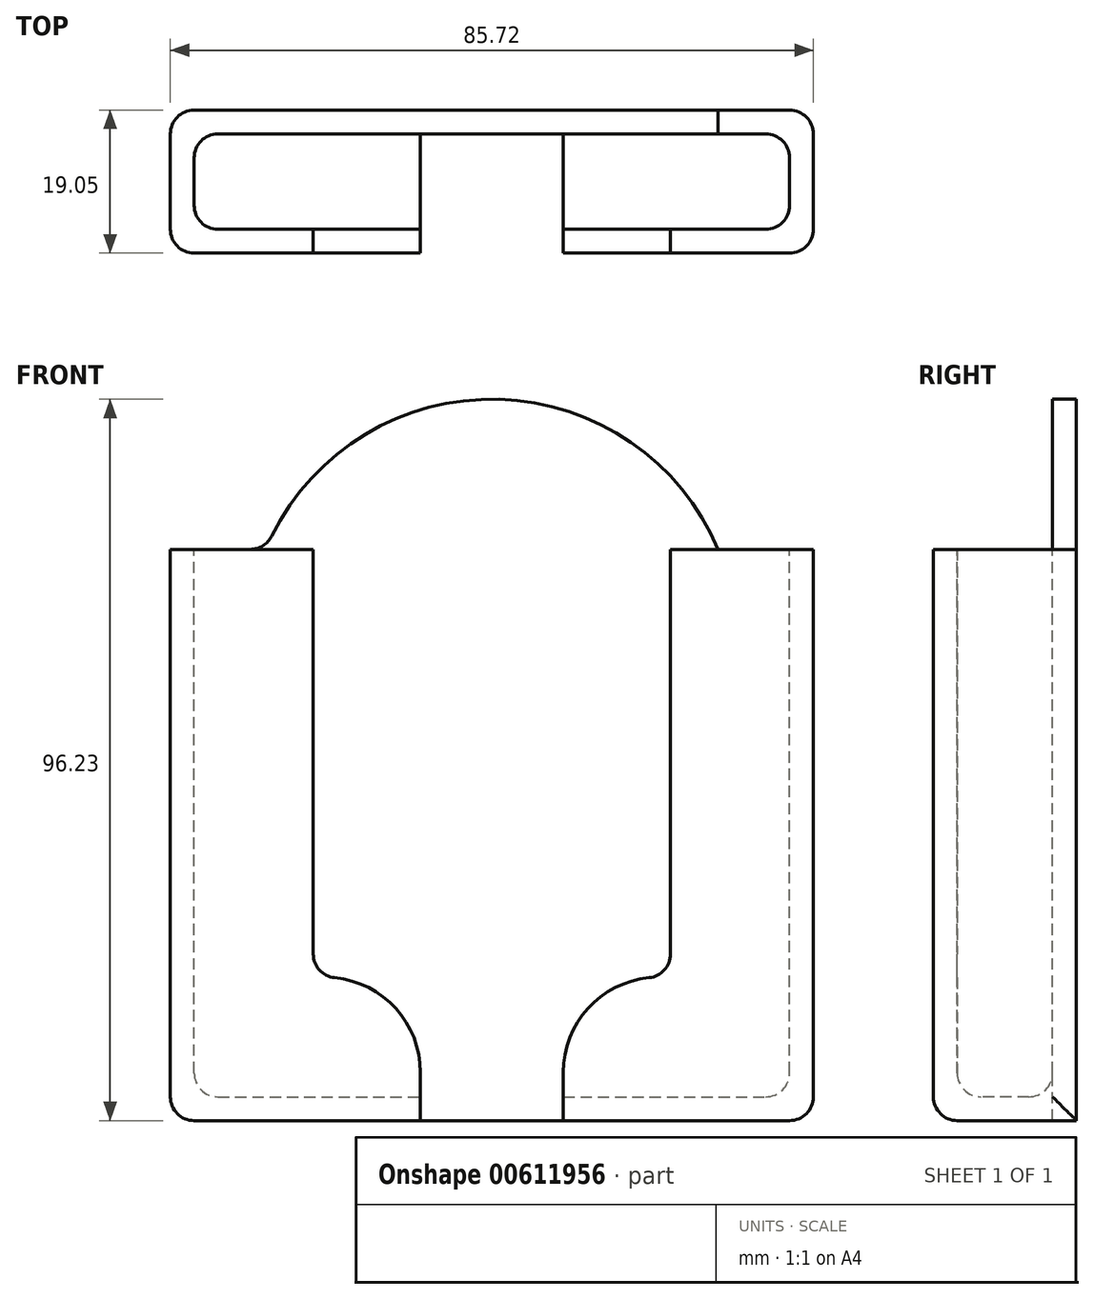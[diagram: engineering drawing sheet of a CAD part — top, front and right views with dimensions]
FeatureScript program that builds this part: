
annotation { "Feature Type Name" : "Feature", "Feature Type Description" : "" }
export const myFeature = defineFeature(function(context is Context, id is Id, definition is map)
    precondition{}
    {
        {
            var Q0;
            Q0=qCreatedBy(makeId("Front.planeOp"),FACE);
            var sketch = newSketch(context, id + "F0", { "sketchPlane" : qUnion([Q0])});
            skLineSegment(sketch, "E0.bottom", {"start": v(0, 0) * mm, "end": v(85.73, 0) * mm});
            skLineSegment(sketch, "E0.top", {"start": v(0, 76.2) * mm, "end": v(85.72, 76.2) * mm});
            skLineSegment(sketch, "E0.left", {"start": v(0, 0) * mm, "end": v(0, 76.2) * mm});
            skLineSegment(sketch, "E0.right", {"start": v(85.73, 0) * mm, "end": v(85.72, 76.2) * mm});
            skSolve(sketch);
        }
        {
            var Q0;
            Q0 = qSketchRegion(id + "F0", true);
            extrude(context, id + "F1", {"entities" : qUnion([Q0]), "depth" : 19.05 * mm, "offsetDistance" : 25.4 * mm});
        }
        {
            var Q0;
            Q0=makeQuery(id+"F1.opExtrude","SWEPT_FACE",FACE,{"disambiguationData":[OSD([sQuery(id+"F0.wireOp",EDGE,"E0.top")])]});
            shell(context, id + "F2", {"entities" : qUnion([Q0]), "thickness" : 3.17 * mm});
        }
        {
            var Q0;
            Q0=makeQuery(id+"F1.opExtrude","CAP_FACE",FACE,{"disambiguationData":[OSD([sQuery(id+"F0.wireOp",EDGE,"E0.bottom"),sQuery(id+"F0.wireOp",EDGE,"E0.top"),sQuery(id+"F0.wireOp",EDGE,"E0.left"),sQuery(id+"F0.wireOp",EDGE,"E0.right")])],"isStart":false});
            var sketch = newSketch(context, id + "F3", { "sketchPlane" : qUnion([Q0])});
            skPoint(sketch, "E1.startSnap0", {"position": v(42.86, 76.2) * mm});
            skLineSegment(sketch, "E2.bottom", {"start": v(19.05, 76.2) * mm, "end": v(42.86, 76.2) * mm});
            skLineSegment(sketch, "E2.top", {"start": v(19.05, 19.05) * mm, "end": v(33.34, 19.05) * mm});
            skLineSegment(sketch, "E2.left", {"start": v(19.05, 76.2) * mm, "end": v(19.05, 19.05) * mm});
            skLineSegment(sketch, "E3.top", {"start": v(33.34, 0) * mm, "end": v(42.86, 0) * mm});
            skLineSegment(sketch, "E3.left", {"start": v(33.34, 19.05) * mm, "end": v(33.34, 0) * mm});
            skLineSegment(sketch, "E4", {"start": v(42.86, 76.2) * mm, "end": v(42.86, 0) * mm});
            skLineSegment(sketch, "E5", {"start": v(42.86, 99.28) * mm, "end": v(42.86, -20.52) * mm, "construction": true});
            skLineSegment(sketch, "E6.MirrorCS", {"start": v(52.39, 19.05) * mm, "end": v(52.39, 0) * mm});
            skLineSegment(sketch, "E7.MirrorCS", {"start": v(66.67, 76.2) * mm, "end": v(66.67, 19.05) * mm});
            skLineSegment(sketch, "E8.MirrorCS", {"start": v(66.67, 19.05) * mm, "end": v(52.39, 19.05) * mm});
            skLineSegment(sketch, "E9.MirrorCS", {"start": v(66.67, 76.2) * mm, "end": v(42.86, 76.2) * mm});
            skLineSegment(sketch, "E10.MirrorCS", {"start": v(52.39, 0) * mm, "end": v(42.86, 0) * mm});
            skSolve(sketch);
        }
        {
            var Q0;
            Q0 = qSketchRegion(id + "F3", true);
            var Q1;
            {var subQ0=sQuery(id+"F0.wireOp",EDGE,"E0.right");var subQ1=sQuery(id+"F0.wireOp",EDGE,"E0.left");var subQ2=sQuery(id+"F0.wireOp",EDGE,"E0.top");var subQ3=sQuery(id+"F0.wireOp",EDGE,"E0.bottom");Q1=makeQuery(id+"F2.opShell","OFFSET_FACE",FACE,{"disambiguationData":[OSD([subQ3,subQ2,subQ1,subQ0]),TDD([makeQuery(id+"F1.opExtrude","CAP_FACE",FACE,{"disambiguationData":[OSD([subQ3,subQ2,subQ1,subQ0])],"isStart":true})])]});}
            extrude(context, id + "F4", {"entities" : qUnion([Q0]), "operationType" : NewBodyOperationType.REMOVE, "endBound" : BoundingType.UP_TO_SURFACE, "oppositeDirection" : true, "depth" : 25.4 * mm, "endBoundEntityFace" : qUnion([Q1]), "offsetDistance" : 25.4 * mm});
        }
        {
            var Q0;
            Q0=makeQuery(id+"F1.opExtrude","CAP_FACE",FACE,{"disambiguationData":[OSD([sQuery(id+"F0.wireOp",EDGE,"E0.bottom"),sQuery(id+"F0.wireOp",EDGE,"E0.top"),sQuery(id+"F0.wireOp",EDGE,"E0.left"),sQuery(id+"F0.wireOp",EDGE,"E0.right")])],"isStart":true});
            var sketch = newSketch(context, id + "F5", { "sketchPlane" : qUnion([Q0])});
            skArc(sketch, "E11", {"start": v(-12.7, 76.2) * mm, "mid": v(-42.86, 96.23) * mm, "end": v(-73.02, 76.2) * mm});
            skSolve(sketch);
        }
        {
            var Q0;
            {var subQ0=sQuery(id+"F5.wireOp",EDGE,"E11");Q0=makeQuery(id+"F5.imprint","IMPRINT",FACE,{"disambiguationData":[TD([[makeQuery(id+"F5.imprint","IMPRINT",EDGE,{"derivedFrom":subQ0}),1.0]])]});}
            var Q1;
            {var subQ0=sQuery(id+"F0.wireOp",EDGE,"E0.right");var subQ1=sQuery(id+"F0.wireOp",EDGE,"E0.left");var subQ2=sQuery(id+"F0.wireOp",EDGE,"E0.top");var subQ3=sQuery(id+"F0.wireOp",EDGE,"E0.bottom");Q1=makeQuery(id+"F4.boolean.opBoolean","MERGE",FACE,{"derivedFrom":[makeQuery(id+"F2.opShell","OFFSET_FACE",FACE,{"disambiguationData":[OSD([subQ3,subQ2,subQ1,subQ0]),TDD([makeQuery(id+"F1.opExtrude","CAP_FACE",FACE,{"disambiguationData":[OSD([subQ3,subQ2,subQ1,subQ0])],"isStart":true})])]}),makeQuery(id+"F4.opExtrude","CAP_FACE",FACE,{"disambiguationData":[OSD([subQ3,subQ2,subQ1,subQ0])],"isStart":false})]});}
            extrude(context, id + "F6", {"entities" : qUnion([Q0]), "operationType" : NewBodyOperationType.ADD, "endBound" : BoundingType.UP_TO_SURFACE, "oppositeDirection" : true, "depth" : 25.4 * mm, "endBoundEntityFace" : qUnion([Q1]), "offsetDistance" : 25.4 * mm});
        }
        {
            var Q0;
            {var subQ0=sQuery(id+"F0.wireOp",EDGE,"E0.left");Q0=makeQuery(id+"F2.opShell","OFFSET_EDGE",EDGE,{"disambiguationData":[OSD([subQ0]),TDD([makeQuery(id+"F1.opExtrude","CAP_EDGE",EDGE,{"disambiguationData":[OSD([subQ0])],"isStart":true})])]});}
            var Q1;
            {var subQ0=sQuery(id+"F0.wireOp",EDGE,"E0.left");Q1=makeQuery(id+"F2.opShell","OFFSET_EDGE",EDGE,{"disambiguationData":[OSD([subQ0]),TDD([makeQuery(id+"F1.opExtrude","CAP_EDGE",EDGE,{"disambiguationData":[OSD([subQ0])],"isStart":false})])]});}
            var Q2;
            {var subQ0=sQuery(id+"F5.wireOp",EDGE,"E11");var subQ1=sQuery(id+"F0.wireOp",EDGE,"E0.top");Q2=makeQuery(id+"F6.opExtrude","SWEPT_EDGE",EDGE,{"disambiguationData":[OSD([subQ1,subQ0]),TDD([makeQuery(id+"F5.imprint","INTERSECT",VERTEX,{"disambiguationData":[OD(0.0)],"derivedFrom":[makeQuery(id+"F1.opExtrude","CAP_EDGE",EDGE,{"disambiguationData":[OSD([subQ1])],"isStart":true}),subQ0]})])]});}
            var Q3;
            {var subQ0=sQuery(id+"F5.wireOp",EDGE,"E11");var subQ1=sQuery(id+"F0.wireOp",EDGE,"E0.top");Q3=makeQuery(id+"F6.opExtrude","SWEPT_EDGE",EDGE,{"disambiguationData":[OSD([subQ1,subQ0]),TDD([makeQuery(id+"F5.imprint","INTERSECT",VERTEX,{"disambiguationData":[OD(1.0)],"derivedFrom":[makeQuery(id+"F1.opExtrude","CAP_EDGE",EDGE,{"disambiguationData":[OSD([subQ1])],"isStart":true}),subQ0]})])]});}
            var Q4;
            {var subQ0=sQuery(id+"F0.wireOp",EDGE,"E0.right");Q4=makeQuery(id+"F2.opShell","OFFSET_EDGE",EDGE,{"disambiguationData":[OSD([subQ0]),TDD([makeQuery(id+"F1.opExtrude","CAP_EDGE",EDGE,{"disambiguationData":[OSD([subQ0])],"isStart":true})])]});}
            var Q5;
            {var subQ0=sQuery(id+"F0.wireOp",EDGE,"E0.right");Q5=makeQuery(id+"F2.opShell","OFFSET_EDGE",EDGE,{"disambiguationData":[OSD([subQ0]),TDD([makeQuery(id+"F1.opExtrude","CAP_EDGE",EDGE,{"disambiguationData":[OSD([subQ0])],"isStart":false})])]});}
            var Q6;
            Q6=makeQuery(id+"F4.boolean.opBoolean","COPY",EDGE,{"derivedFrom":makeQuery(id+"F4.opExtrude","SWEPT_EDGE",EDGE,{"disambiguationData":[OSD([sQuery(id+"F3.wireOp",EDGE,"E7.MirrorCS"),sQuery(id+"F3.wireOp",EDGE,"E8.MirrorCS")])]})});
            var Q7;
            Q7=makeQuery(id+"F4.boolean.opBoolean","COPY",EDGE,{"derivedFrom":makeQuery(id+"F4.opExtrude","SWEPT_EDGE",EDGE,{"disambiguationData":[OSD([sQuery(id+"F3.wireOp",EDGE,"E2.top"),sQuery(id+"F3.wireOp",EDGE,"E2.left")])]})});
            var Q8;
            {var subQ1=sQuery(id+"F0.wireOp",EDGE,"E0.left");var subQ3=sQuery(id+"F0.wireOp",EDGE,"E0.bottom");Q8=makeQuery(id+"F4.boolean.opBoolean","SPLIT",EDGE,{"disambiguationData":[TD([makeQuery(id+"F2.opShell","OFFSET_FACE",FACE,{"disambiguationData":[OSD([subQ1])]})])],"derivedFrom":makeQuery(id+"F2.opShell","OFFSET_EDGE",EDGE,{"disambiguationData":[OSD([subQ3]),TDD([makeQuery(id+"F1.opExtrude","CAP_EDGE",EDGE,{"disambiguationData":[OSD([subQ3])],"isStart":true})])]})});}
            var Q9;
            Q9=makeQuery(id+"F2.opShell","OFFSET_EDGE",EDGE,{"disambiguationData":[OSD([sQuery(id+"F0.wireOp",EDGE,"E0.bottom"),sQuery(id+"F0.wireOp",EDGE,"E0.left")])]});
            var Q10;
            {var subQ0=sQuery(id+"F0.wireOp",EDGE,"E0.bottom");var subQ2=sQuery(id+"F0.wireOp",EDGE,"E0.left");Q10=makeQuery(id+"F4.boolean.opBoolean","SPLIT",EDGE,{"disambiguationData":[TD([makeQuery(id+"F2.opShell","OFFSET_FACE",FACE,{"disambiguationData":[OSD([subQ2])]})])],"derivedFrom":makeQuery(id+"F2.opShell","OFFSET_EDGE",EDGE,{"disambiguationData":[OSD([subQ0]),TDD([makeQuery(id+"F1.opExtrude","CAP_EDGE",EDGE,{"disambiguationData":[OSD([subQ0])],"isStart":false})])]})});}
            var Q11;
            {var subQ0=sQuery(id+"F0.wireOp",EDGE,"E0.right");var subQ3=sQuery(id+"F0.wireOp",EDGE,"E0.bottom");Q11=makeQuery(id+"F4.boolean.opBoolean","SPLIT",EDGE,{"disambiguationData":[TD([makeQuery(id+"F2.opShell","OFFSET_FACE",FACE,{"disambiguationData":[OSD([subQ0])]})])],"derivedFrom":makeQuery(id+"F2.opShell","OFFSET_EDGE",EDGE,{"disambiguationData":[OSD([subQ3]),TDD([makeQuery(id+"F1.opExtrude","CAP_EDGE",EDGE,{"disambiguationData":[OSD([subQ3])],"isStart":true})])]})});}
            var Q12;
            {var subQ0=sQuery(id+"F0.wireOp",EDGE,"E0.bottom");var subQ1=sQuery(id+"F0.wireOp",EDGE,"E0.right");Q12=makeQuery(id+"F4.boolean.opBoolean","SPLIT",EDGE,{"disambiguationData":[TD([makeQuery(id+"F2.opShell","OFFSET_FACE",FACE,{"disambiguationData":[OSD([subQ1])]})])],"derivedFrom":makeQuery(id+"F2.opShell","OFFSET_EDGE",EDGE,{"disambiguationData":[OSD([subQ0]),TDD([makeQuery(id+"F1.opExtrude","CAP_EDGE",EDGE,{"disambiguationData":[OSD([subQ0])],"isStart":false})])]})});}
            var Q13;
            Q13=makeQuery(id+"F2.opShell","OFFSET_EDGE",EDGE,{"disambiguationData":[OSD([sQuery(id+"F0.wireOp",EDGE,"E0.bottom"),sQuery(id+"F0.wireOp",EDGE,"E0.right")])]});
            var Q14;
            Q14=makeQuery(id+"F1.opExtrude","CAP_EDGE",EDGE,{"disambiguationData":[OSD([sQuery(id+"F0.wireOp",EDGE,"E0.right")])],"isStart":false});
            var Q15;
            Q15=makeQuery(id+"F1.opExtrude","CAP_EDGE",EDGE,{"disambiguationData":[OSD([sQuery(id+"F0.wireOp",EDGE,"E0.right")])],"isStart":true});
            var Q16;
            Q16=makeQuery(id+"F1.opExtrude","CAP_EDGE",EDGE,{"disambiguationData":[OSD([sQuery(id+"F0.wireOp",EDGE,"E0.left")])],"isStart":true});
            var Q17;
            Q17=makeQuery(id+"F1.opExtrude","CAP_EDGE",EDGE,{"disambiguationData":[OSD([sQuery(id+"F0.wireOp",EDGE,"E0.left")])],"isStart":false});
            var Q18;
            Q18=makeQuery(id+"F1.opExtrude","SWEPT_EDGE",EDGE,{"disambiguationData":[OSD([sQuery(id+"F0.wireOp",EDGE,"E0.bottom"),sQuery(id+"F0.wireOp",EDGE,"E0.left")])]});
            var Q19;
            {var subQ0=sQuery(id+"F0.wireOp",EDGE,"E0.bottom");var subQ1=sQuery(id+"F0.wireOp",EDGE,"E0.right");Q19=makeQuery(id+"F4.boolean.opBoolean","SPLIT",EDGE,{"disambiguationData":[TD([makeQuery(id+"F1.opExtrude","SWEPT_FACE",FACE,{"disambiguationData":[OSD([subQ1])]})])],"derivedFrom":makeQuery(id+"F1.opExtrude","CAP_EDGE",EDGE,{"disambiguationData":[OSD([subQ0])],"isStart":false})});}
            var Q20;
            {var subQ0=sQuery(id+"F0.wireOp",EDGE,"E0.bottom");var subQ1=sQuery(id+"F0.wireOp",EDGE,"E0.left");Q20=makeQuery(id+"F4.boolean.opBoolean","SPLIT",EDGE,{"disambiguationData":[TD([makeQuery(id+"F1.opExtrude","SWEPT_FACE",FACE,{"disambiguationData":[OSD([subQ1])]})])],"derivedFrom":makeQuery(id+"F1.opExtrude","CAP_EDGE",EDGE,{"disambiguationData":[OSD([subQ0])],"isStart":false})});}
            var Q21;
            Q21=makeQuery(id+"F1.opExtrude","SWEPT_EDGE",EDGE,{"disambiguationData":[OSD([sQuery(id+"F0.wireOp",EDGE,"E0.bottom"),sQuery(id+"F0.wireOp",EDGE,"E0.right")])]});
            fillet(context, id + "F7", {"entities" : qUnion([Q0, Q1, Q2, Q3, Q4, Q5, Q6, Q7, Q8, Q9, Q10, Q11, Q12, Q13, Q14, Q15, Q16, Q17, Q18, Q19, Q20, Q21]), "radius" : 3.17 * mm, "tangentPropagation" : true, "allowEdgeOverflow" : false});
        }
        {
            var Q0;
            Q0=makeQuery(id+"F4.boolean.opBoolean","COPY",EDGE,{"derivedFrom":makeQuery(id+"F4.opExtrude","SWEPT_EDGE",EDGE,{"disambiguationData":[OSD([sQuery(id+"F0.wireOp",EDGE,"E0.top"),sQuery(id+"F3.wireOp",EDGE,"E2.bottom"),sQuery(id+"F3.wireOp",EDGE,"E2.left")])]})});
            var Q1;
            Q1=makeQuery(id+"F4.boolean.opBoolean","COPY",EDGE,{"derivedFrom":makeQuery(id+"F4.opExtrude","SWEPT_EDGE",EDGE,{"disambiguationData":[OSD([sQuery(id+"F0.wireOp",EDGE,"E0.top"),sQuery(id+"F3.wireOp",EDGE,"E7.MirrorCS"),sQuery(id+"F3.wireOp",EDGE,"E9.MirrorCS")])]})});
            var Q2;
            Q2=makeQuery(id+"F4.boolean.opBoolean","COPY",EDGE,{"derivedFrom":makeQuery(id+"F4.opExtrude","SWEPT_EDGE",EDGE,{"disambiguationData":[OSD([sQuery(id+"F3.wireOp",EDGE,"E6.MirrorCS"),sQuery(id+"F3.wireOp",EDGE,"E8.MirrorCS")])]})});
            var Q3;
            Q3=makeQuery(id+"F4.boolean.opBoolean","COPY",EDGE,{"derivedFrom":makeQuery(id+"F4.opExtrude","SWEPT_EDGE",EDGE,{"disambiguationData":[OSD([sQuery(id+"F3.wireOp",EDGE,"E2.top"),sQuery(id+"F3.wireOp",EDGE,"E3.left")])]})});
            fillet(context, id + "F8", {"entities" : qUnion([Q0, Q1, Q2, Q3]), "radius" : 12.7 * mm, "tangentPropagation" : true, "allowEdgeOverflow" : false});
        }
    });
